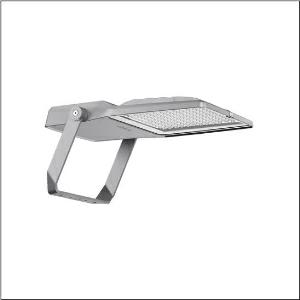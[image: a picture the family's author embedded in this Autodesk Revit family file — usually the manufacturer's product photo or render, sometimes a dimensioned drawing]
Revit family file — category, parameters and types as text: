
# Revit family: floodlight_fl_21_iq_midi___rs12_5xa7782f2b1a_e9cf
name_source: partatom
category: Lighting Fixtures
units: mm (PartAtom-declared; Revit-internal decimal feet)

## family parameters
Cut with Voids When Loaded = No
Host = Face
Light Source = No
Part Type = Normal
Room Calculation Point = No
Round Connector Dimension = Use Diameter
Shared = No

## types (1)
- --- (1 x LED, 35590 lm, 270.2 W, 3000K)
    Apparent Load = 270 VA
    CIE Flux Codes = 79 92 99 100 100
    Color Rendering = 70
    Color Temperature = 3000K
    Default Elevation = 1800 mm
    Description = Floodlight FL 21 iQ midi, floodlight, primary light control with lens, of PMMA, primary optical cover: protective disc, of toughened safety glass, transparent, light distribution: RS12, light emission: direct distribution, installation type: surface-mounted, LED, High Power LED, rated luminous flux: 35.590lm, luminous efficacy: 132lm/W, light colour: 730, colour temperature: 3000K, control gear: ECG iQ, control: optimised constant luminous flux control (CLO 2.0), Desk-Remote (wireless, voltage-free reading and setting of iQ features in the workshop via application-optimized NFC function/RFID function), Smart-Wire, Night-Set, Temp-Guard, Street-Remote, Auto-Match, with terminal, 6-pole, mains connection: 220..240V, AC, 50/60Hz, start of lifetime: 270W, end of service life: 287W, reduction: 117W, luminaire housing, of diecast aluminium, powder-coated, Siteco® metallic grey (DB 702S), corrosivity category C5 mid according to DIN EN ISO 12944, sealing non-destructively replaceable, mounting bracket, of steel, galvanised, powder-coated, Siteco® metallic grey (DB 702S), protection rating (complete): IP66, insulation class (complete): insulation class II (safety insulation), certification: CE, protection symbol: D, impact resistance: IK08, permissible operating ambient temperature: -40..+40°C, permissible operating ambient temperature for outdoor applications: -40..+50°C, standard: DIN EN 12944, LABS conformity tested according to VDMA 24364:2018-05, packaging unit: 1 piece

Light Distribution: RS12
    Height = 76 mm
    Lamp = 1 x LED
    Lamp Light Flux = 35590 lm
    Lamp Power = 270.2 W
    Lamp count = 1
    Length = 657 mm
    Luminous efficacy = 132 lm/W
    Manufacturer = Siteco
    ModVariant = No
    Model = 5XA7782F2B1A
    Number of Poles = 1
    OnlyDefault = Yes
    Power Factor = 1
    Product Name = Floodlight FL 21 iQ midi | RS12
    Product group = floodlight | pylon annexe
    ProductGroupID = 6200
    Protection Class = Protection class II
    Protection Degree = IP 66
    RLX_Detail_Level = 1
    RLX_Emergency_Light_Flux = 0 lm
    RLX_Emergency_Type = 0
    RLX_Emergency_Type_DB = No
    RlxData = <blob elided: 141253 chars, md5=7d476d7e>
    Socket = socket
    Standby Power = 0 W
    System Light Flux = 35590 lm
    System Power = 270 W
    Type Comments = factory setting: luminous flux: 100 % | dim-lin: 254 | 620 mA
    Type Image = l_1006876.jpg
    URL = http://relux.com
    VarID = @adj_037641
    Voltage = 0 V
    Weight = 0.00 kg
    Width = 442 mm

## geometry (parser evidence)
native form markers: Blend x4, Sweep x15
no freeform markers — native parametric forms only
